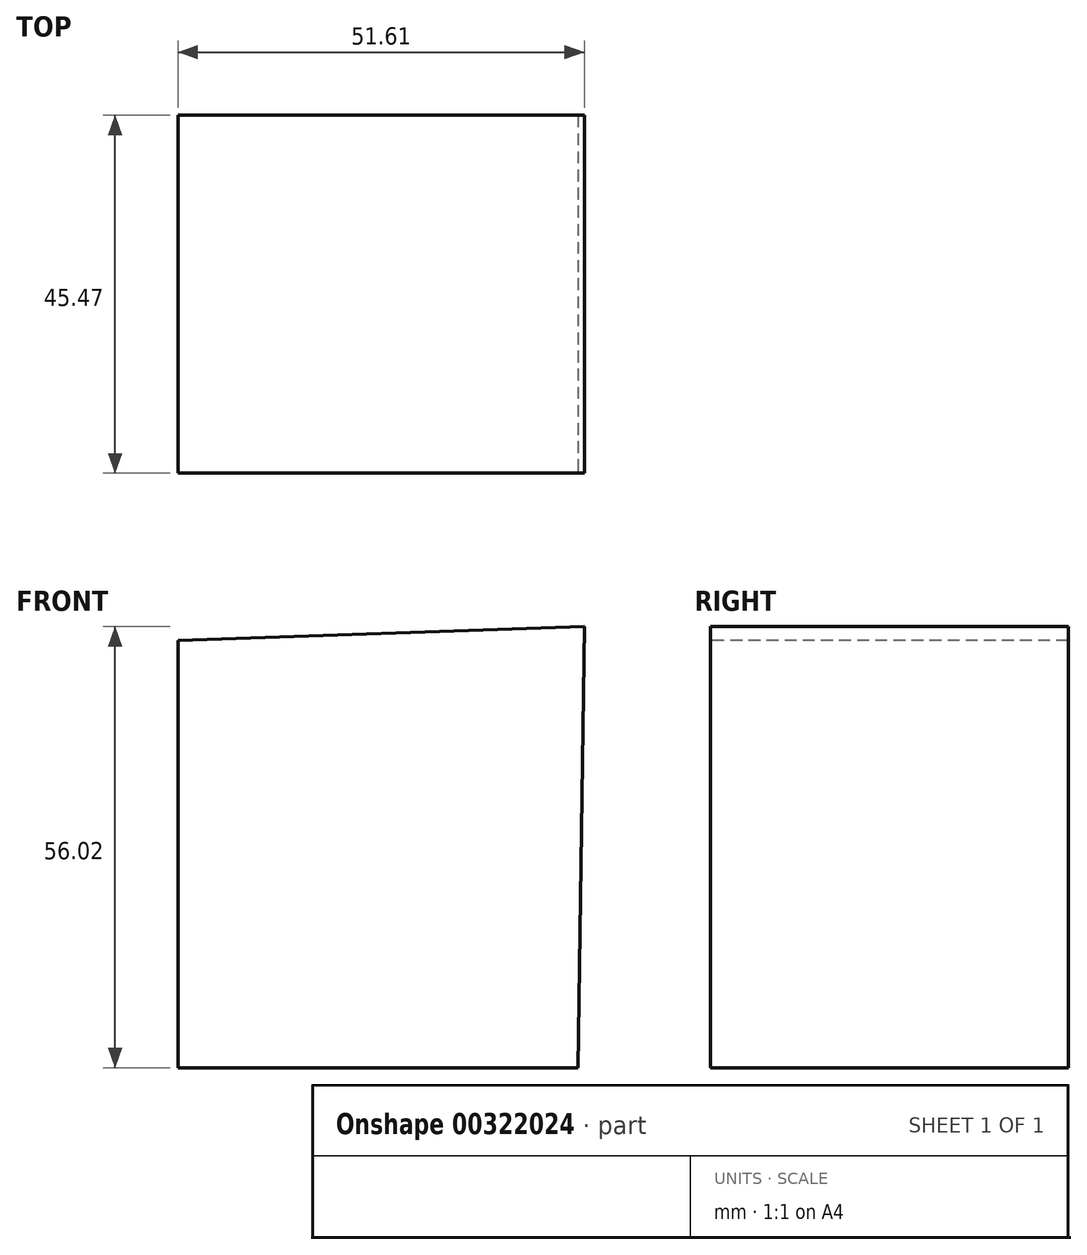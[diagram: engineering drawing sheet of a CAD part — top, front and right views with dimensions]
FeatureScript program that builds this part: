
annotation { "Feature Type Name" : "Feature", "Feature Type Description" : "" }
export const myFeature = defineFeature(function(context is Context, id is Id, definition is map)
    precondition{}
    {
        {
            var Q0;
            Q0=qCreatedBy(makeId("Front.planeOp"),FACE);
            var sketch = newSketch(context, id + "F0", { "sketchPlane" : qUnion([Q0])});
            skLineSegment(sketch, "E0", {"start": v(-51.6, 33.2) * mm, "end": v(-51.6, -21.06) * mm});
            skLineSegment(sketch, "E1", {"start": v(-51.6, -21.06) * mm, "end": v(-0.8, -21.06) * mm});
            skLineSegment(sketch, "E2", {"start": v(-0.8, -21.06) * mm, "end": v(0, 34.96) * mm});
            skLineSegment(sketch, "E3", {"start": v(0, 34.96) * mm, "end": v(-51.6, 33.2) * mm});
            skSolve(sketch);
        }
        {
            var Q0;
            Q0=makeQuery(id+"F0.imprint","IMPRINT",FACE,{"disambiguationData":[TD([[makeQuery(id+"F0.imprint","IMPRINT",EDGE,{"derivedFrom":sQuery(id+"F0.wireOp",EDGE,"E0")}),1.0]])]});
            extrude(context, id + "F1", {"entities" : qUnion([Q0]), "oppositeDirection" : true, "depth" : 45.47 * mm});
        }
    });
